# Revit family: Backflow_Preventer-RP-Zurn_Wilkins_Model_475STDA_Flanged (4-10_inch)
name_source: partatom
category: Pipe Accessories
units: mm (PartAtom-declared; Revit-internal decimal feet)

## family parameters
Always vertical = Yes
Cut with Voids When Loaded = No
Part Type = Valve - Breaks Into
Round Connector Dimension = Use Radius
Shared = No
Work Plane-Based = No

## types (4) — shared parameters
Assembly Code = D2020300
Center to end for fixing gate valve = 0' - 0"
DA Length = 1' - 0"
Default Elevation = 0' - 0"
Description = Reduced Pressure Detector Assembly
Flow Rate (GPM) = 0 GPM
Height = 1' - 0"
Hydrostatic test pressure = 350.00 psi
Length = 2' - 0"
Main Material = Paint - Zurn - Stainless steel
Manufacturer = Zurn Water, LLC
Manufacturer Brand = Zurn Wilkins
Max Working Water Pressure = 175.00 psi
Max Working Water Temperature = 140 °F
Model = 475STDA
Modified Data = 11/10/2025
Product Documentation Link = https://files.zurn.com
Product Installation Sheet URL = https://files.zurn.com
Product Page URL = https://www.zurn.com
Product data URL = https://www.bimobject.com
Repair Parts URL = https://files.zurn.com
URL = www.zurn.com
Width = 1' - 0"

## per-type parameters (varying)
| type | Center to bottom coupling | Center to main valve center | Center to top of ball on top | DA MR Height | DA MR Length | DIM A - Inlet center to outlet center | DIM B - Overall height of the valve | DIM C - Valve center to gate stem top | DIM D - Valve center to side coupling end | DIM E - Valve top to bottom of relief valve | Fitting Bottom end | Fitting Height | Fitting Length | Gate Valve | Inlet to relief valve center | Main Valve | Nominal Diameter | Nominal Radius | Product Weight (lbs) | Relief valve |
| 4-475STDA (4" 475STDA) | 0' - 6" | 0' - 0" | 0' - 7 1/4" | 0' - 11" | 2' - 1 1/2" | 1' - 2" | 1' - 10 1/4" | 1' - 10 1/2" | 0' - 10 1/8" | 1' - 6 3/8" | 1' - 4" | 1' - 0 1/2" | 1' - 8" | Gate Valve_475_OSY : 4" | 0' - 5 31/32" | Zurn_Wilkins_Model_450ST-(4_Inch) : 4 inch | 0' - 4" | 0' - 2" | 215 | Zurn_Wilkins-Model-3707-CU-XL : 4" |
| 6-475STDA (6" 475STDA) | 0' - 7 9/16" | 0' - 1 9/16" | 0' - 9 13/16" | 0' - 11 1/2" | 2' - 5 1/2" | 1' - 4" | 2' - 3 7/8" | 2' - 6 1/2" | 0' - 10 5/8" | 1' - 10 3/8" | 1' - 8" | 1' - 1 1/4" | 2' - 0" | Gate Valve_475_OSY : 6" | 0' - 6 31/32" | Zurn_Wilkins_Model_450ST-(4_Inch) : 6" | 0' - 6" | 0' - 3" | 343 | Zurn_Wilkins-Model-3707-CU-XL : 6" |
| 8-475STDA (8" 475STDA) | 0' - 9 5/8" | 0' - 1 9/16" | 1' - 1 3/4" | 1' - 2" | 2' - 11 1/2" | 1' - 6 1/2" | 2' - 10 7/8" | 3' - 1" | 1' - 0 7/8" | 2' - 6 5/8" | 2' - 0" | 1' - 4 1/2" | 2' - 6" | Gate Valve_475_OSY : 8" | 0' - 8 15/32" | Zurn_Wilkins_Model_450ST-(4_Inch) : 8" | 0' - 8" | 0' - 4" | 594 | Zurn_Wilkins-Model-3707-CU-XL : 8" |
| 10-475STDA (10" 475STDA) | 0' - 10" | 0' - 1 9/16" | 1' - 3 3/4" | 1' - 2" | 3' - 2 1/2" | 1' - 9" | 3' - 2 3/4" | 3' - 9 5/8" | 1' - 0 7/8" | 2' - 8 3/4" | 2' - 0" | 1' - 5" | 2' - 9" | Gate Valve_475_OSY : 10" | 0' - 10 7/32" | Zurn_Wilkins_Model_450ST-(4_Inch) : 10" | 0' - 10" | 0' - 5" | 837 | Zurn_Wilkins-Model-3707-CU-XL : 10 |

## geometry (parser evidence)
native form markers: Blend x7, Sweep x21
no freeform markers — native parametric forms only
